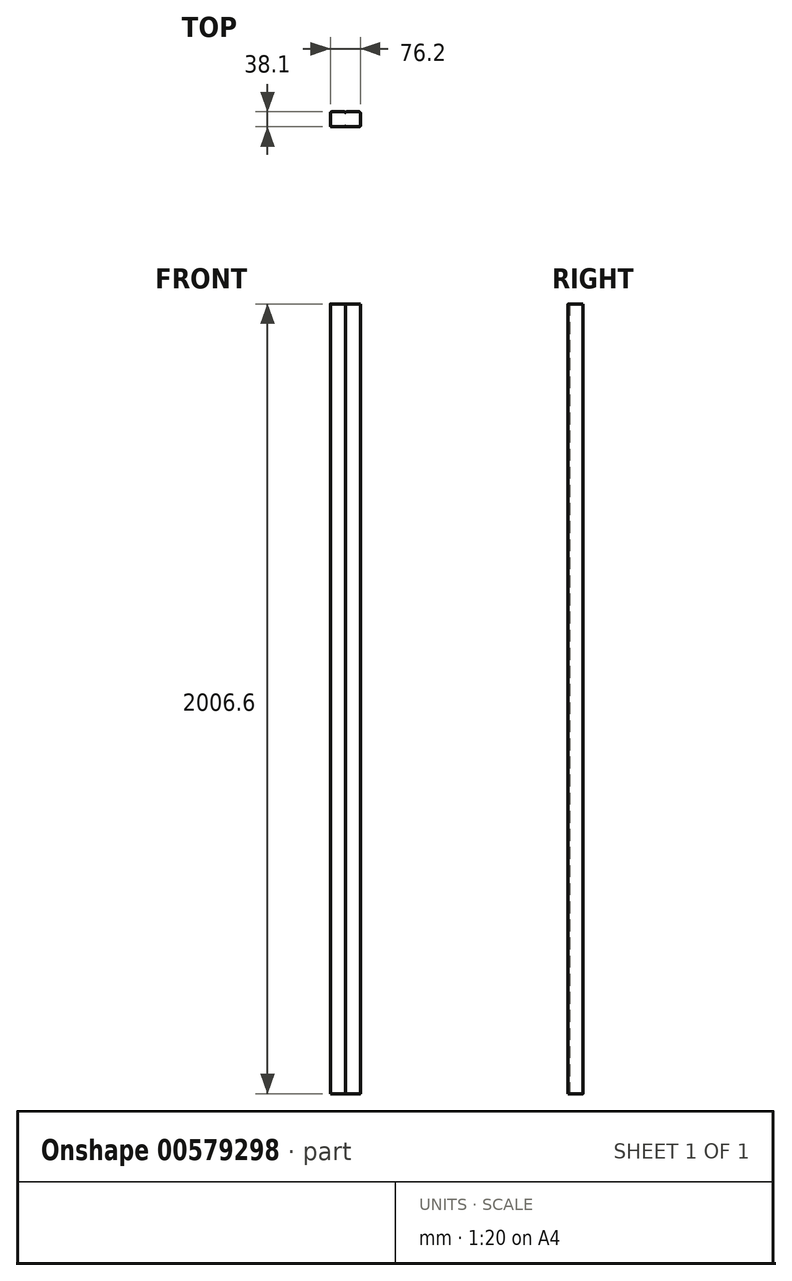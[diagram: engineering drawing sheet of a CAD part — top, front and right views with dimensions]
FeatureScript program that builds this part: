
annotation { "Feature Type Name" : "Feature", "Feature Type Description" : "" }
export const myFeature = defineFeature(function(context is Context, id is Id, definition is map)
    precondition{}
    {
        {
            var Q0;
            Q0=qCreatedBy(makeId("Top.planeOp"),FACE);
            var sketch = newSketch(context, id + "F0", { "sketchPlane" : qUnion([Q0])});
            skLineSegment(sketch, "E0.bottom", {"start": v(34.93, 19.05) * mm, "end": v(3.18, 19.05) * mm});
            skLineSegment(sketch, "E0.top", {"start": v(34.93, -19.05) * mm, "end": v(3.18, -19.05) * mm});
            skLineSegment(sketch, "E0.left", {"start": v(38.1, 15.88) * mm, "end": v(38.1, -15.87) * mm});
            skLineSegment(sketch, "E0.right", {"start": v(-38.1, 15.88) * mm, "end": v(-38.1, -15.88) * mm});
            skPoint(sketch, "E0.middle", {"position": v(0, 0) * mm});
            skLineSegment(sketch, "E1", {"start": v(0, 15.88) * mm, "end": v(0, -15.88) * mm});
            skPoint(sketch, "E2.newPointA", {"position": v(0, 19.05) * mm});
            skPoint(sketch, "E2.newPointB", {"position": v(-38.1, 19.05) * mm});
            skArc(sketch, "E2.filletArc", {"start": v(3.18, 19.05) * mm, "mid": v(0.93, 18.12) * mm, "end": v(0, 15.88) * mm});
            skPoint(sketch, "E3.visualSharp", {"position": v(38.1, 19.05) * mm});
            skArc(sketch, "E3.filletArc", {"start": v(38.1, 15.88) * mm, "mid": v(37.17, 18.12) * mm, "end": v(34.93, 19.05) * mm});
            skPoint(sketch, "E4.visualSharp", {"position": v(38.1, -19.05) * mm});
            skArc(sketch, "E4.filletArc", {"start": v(34.93, -19.05) * mm, "mid": v(37.17, -18.12) * mm, "end": v(38.1, -15.87) * mm});
            skPoint(sketch, "E5.newPointA", {"position": v(-38.1, -19.05) * mm});
            skPoint(sketch, "E5.newPointB", {"position": v(0, -19.05) * mm});
            skArc(sketch, "E5.filletArc", {"start": v(0, -15.88) * mm, "mid": v(0.93, -18.12) * mm, "end": v(3.17, -19.05) * mm});
            skLineSegment(sketch, "E6.bottom", {"start": v(-34.93, 19.05) * mm, "end": v(-3.18, 19.05) * mm});
            skLineSegment(sketch, "E6.top", {"start": v(-34.93, -19.05) * mm, "end": v(-3.18, -19.05) * mm});
            skArc(sketch, "E7.filletArc", {"start": v(-34.93, 19.05) * mm, "mid": v(-37.17, 18.12) * mm, "end": v(-38.1, 15.88) * mm});
            skArc(sketch, "E8.filletArc", {"start": v(0, 15.88) * mm, "mid": v(-0.93, 18.12) * mm, "end": v(-3.18, 19.05) * mm});
            skArc(sketch, "E9.filletArc", {"start": v(-3.18, -19.05) * mm, "mid": v(-0.93, -18.12) * mm, "end": v(0, -15.88) * mm});
            skArc(sketch, "E10.filletArc", {"start": v(-38.1, -15.88) * mm, "mid": v(-37.17, -18.12) * mm, "end": v(-34.93, -19.05) * mm});
            skSolve(sketch);
        }
        {
            var Q0;
            Q0=qSketchRegion(id+"F0",true);
            extrude(context, id + "F1", {"entities" : qUnion([Q0]), "depth" : 2006.6 * mm, "offsetDistance" : 25.4 * mm});
        }
    });
